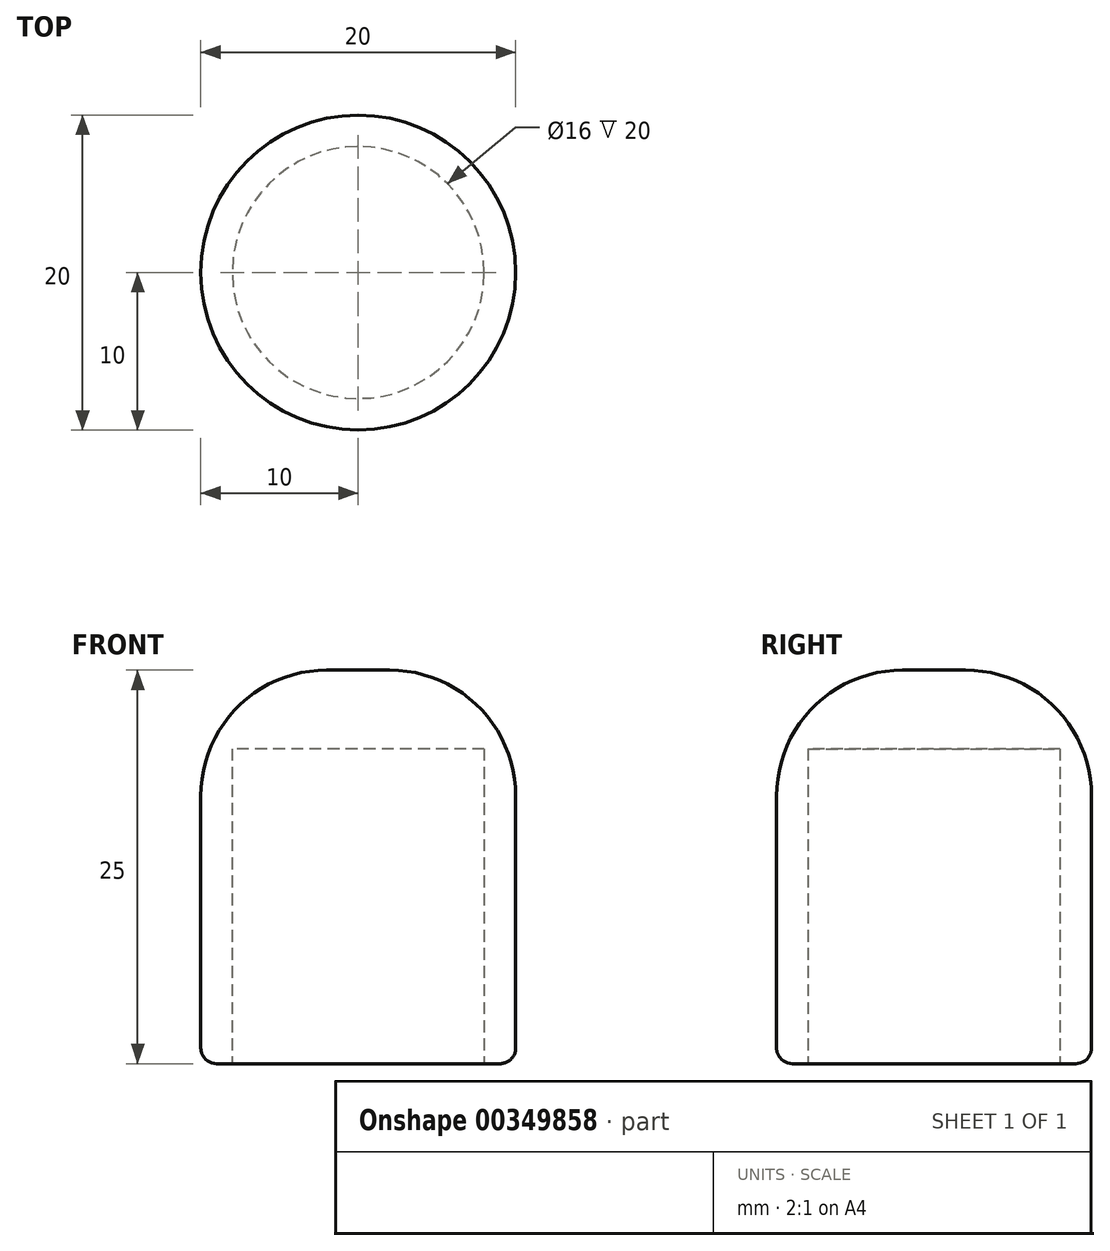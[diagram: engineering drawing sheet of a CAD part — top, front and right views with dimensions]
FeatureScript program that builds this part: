
annotation { "Feature Type Name" : "Feature", "Feature Type Description" : "" }
export const myFeature = defineFeature(function(context is Context, id is Id, definition is map)
    precondition{}
    {
        {
            var Q0;
            Q0=qCreatedBy(makeId("Top.planeOp"),FACE);
            var sketch = newSketch(context, id + "F0", { "sketchPlane" : qUnion([Q0])});
            skCircle(sketch, "E0", {"center": v(0, 0) * mm, "radius": 8 * mm});
            skCircle(sketch, "E1", {"center": v(0, 0) * mm, "radius": 10 * mm});
            skSolve(sketch);
        }
        {
            var Q0;
            Q0=makeQuery(id+"F0.imprint","IMPRINT",FACE,{"disambiguationData":[TD([[makeQuery(id+"F0.imprint","IMPRINT",EDGE,{"derivedFrom":sQuery(id+"F0.wireOp",EDGE,"E0")}),1.0]])]});
            var Q1;
            Q1=makeQuery(id+"F0.imprint","IMPRINT",FACE,{"disambiguationData":[TD([[makeQuery(id+"F0.imprint","IMPRINT",EDGE,{"derivedFrom":sQuery(id+"F0.wireOp",EDGE,"E0")}),-1.0]])]});
            extrude(context, id + "F1", {"entities" : qUnion([Q0, Q1]), "depth" : 25 * mm});
        }
        {
            var Q0;
            Q0=makeQuery(id+"F0.imprint","IMPRINT",FACE,{"disambiguationData":[TD([[makeQuery(id+"F0.imprint","IMPRINT",EDGE,{"derivedFrom":sQuery(id+"F0.wireOp",EDGE,"E0")}),1.0]])]});
            extrude(context, id + "F2", {"entities" : qUnion([Q0]), "operationType" : NewBodyOperationType.REMOVE, "depth" : 20 * mm});
        }
        {
            var Q0;
            Q0=makeQuery(id+"F1.opExtrude","CAP_EDGE",EDGE,{"disambiguationData":[OSD([sQuery(id+"F0.wireOp",EDGE,"E1")])],"isStart":false});
            fillet(context, id + "F3", {"entities" : qUnion([Q0]), "radius" : 8 * mm, "tangentPropagation" : true, "allowEdgeOverflow" : false});
        }
        {
            var Q0;
            Q0=makeQuery(id+"F1.opExtrude","CAP_EDGE",EDGE,{"disambiguationData":[OSD([sQuery(id+"F0.wireOp",EDGE,"E1")])],"isStart":true});
            fillet(context, id + "F4", {"entities" : qUnion([Q0]), "radius" : 1 * mm, "tangentPropagation" : true, "allowEdgeOverflow" : false});
        }
    });
